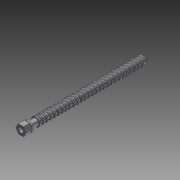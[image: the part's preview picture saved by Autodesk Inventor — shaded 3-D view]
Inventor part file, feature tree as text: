
AUTODESK INVENTOR PART (.ipt)
format: ipt  version: 2012 (Build 160160000, 160)  size: 2,206,720 bytes
history: native  units: in
note: dims shown in document units (in); Inventor stores cm internally (conversion verified against a paired STEP export)
features: sketch x15, extrude x14, plane x10, fillet x5, projected_geometry x2, helix x1, chamfer x1
ambient origin geometry x8: Origin, YZ Plane, XZ Plane, XY Plane, X Axis, Y Axis, Z Axis, Center Point
feature tree (48):
  plane  "Work Plane2"
  plane  "Work Plane5"
  plane  "Work Plane6"
  extrude  "Extrusion2"  Depth=0.3937in TaperAngle=0.0deg
  sketch  "Sketch9"  dims[d33=6.674in d34=0.0in d37=0.1969in]
  plane  "Work Plane7"
  extrude  "Extrusion7"  Depth=0.1969in
  plane  "Work Plane10"
  sketch  "Sketch10"  dims[d56=0.5512in d57=0.3937in d58=0.0in]
  sketch  "Sketch11"  dims[d60=0.1181in d61=0.2362in]
  plane  "Work Plane8"
  extrude  "Extrusion9"  Depth=0.3937in TaperAngle=0.0deg
  plane  "Work Plane9"
  plane  "Work Plane11"
  extrude  "Extrusion10"  Depth=0.2362in
  extrude  "Extrusion13"  Depth=0.3937in
  fillet  "Fillet10"  Radius=0.1181in
  helix  "Coil2"  [1 undecoded]
  chamfer  "Chamfer1"  Distance=0.1181in
  plane  "Work Plane12"
  extrude  "Extrusion12"  Depth=0.0787in
  fillet  "Fillet7"  Radius=0.0118in
  extrude  "Extrusion16"  Depth=0.4134in TaperAngle=0.0deg
  extrude  "Extrusion17"  Depth=0.0118in TaperAngle=0.0deg
  extrude  "Extrusion18"  Depth=0.0394in
  extrude  "Extrusion19"  Depth=0.0059in
  fillet  "Fillet17"  Radius=0.3937in
  fillet  "Fillet18"  Radius=0.2756in
  extrude  "Extrusion20"  Depth=0.3937in TaperAngle=0.0deg
  extrude  "Extrusion21"  Depth=0.3937in TaperAngle=0.0deg
  plane  "Work Plane14"
  extrude  "Extrusion23"  [1 undecoded]
  fillet  "Fillet19"  [1 undecoded]
  extrude  "Extrusion24"  [1 undecoded]
  sketch  "Sketch4"  dims[d5=0.5in d6=0.0in d27=0.3937in d28=0.0in]
  projected_geometry  "Projected Loop3"
  sketch  "Sketch14"  dims[d62=0.3937in d63=11.0236in d64=0.0in d65=90.0deg d66=90.0deg d67=0.0in d68=0.0in d75=0.3937in d76=0.1181in d77=0.1181in d78=0.0in]
  sketch  "Sketch16"  dims[d79=0.0197in]
  sketch  "Sketch17"  dims[d81=0.6398in d82=0.1181in d83=0.0in]
  sketch  "Sketch25"  dims[d89=0.0787in d96=0.0787in d97=0.0492in d98=0.481in d103=0.0118in d104=0.0in]
  sketch  "Sketch26"  dims[d105=0.0118in d106=0.0in d107=0.4134in d108=0.0in]
  projected_geometry  "Projected Loop11"
  sketch  "Sketch27"  dims[d109=0.0118in d110=0.0in d111=0.0118in d112=0.0in]
  sketch  "Sketch28"  dims[d113=0.0787in d114=0.0394in]
  sketch  "Sketch29"  dims[d115=0.0394in d116=0.0059in d117=0.3937in d118=0.0in d119=0.2756in]
  sketch  "Sketch30"  dims[d120=0.1969in d121=0.0in d124=0.3937in d125=0.0in]
  sketch  "Sketch32"  dims[d126=0.0394in d127=0.3937in d128=0.0in]
  sketch  "Sketch33"
note: 4 required parameter values undecoded (feature->parameter linkage not recoverable at this tier; creation-order binding heuristic only, values carry confidence <= 0.55)
